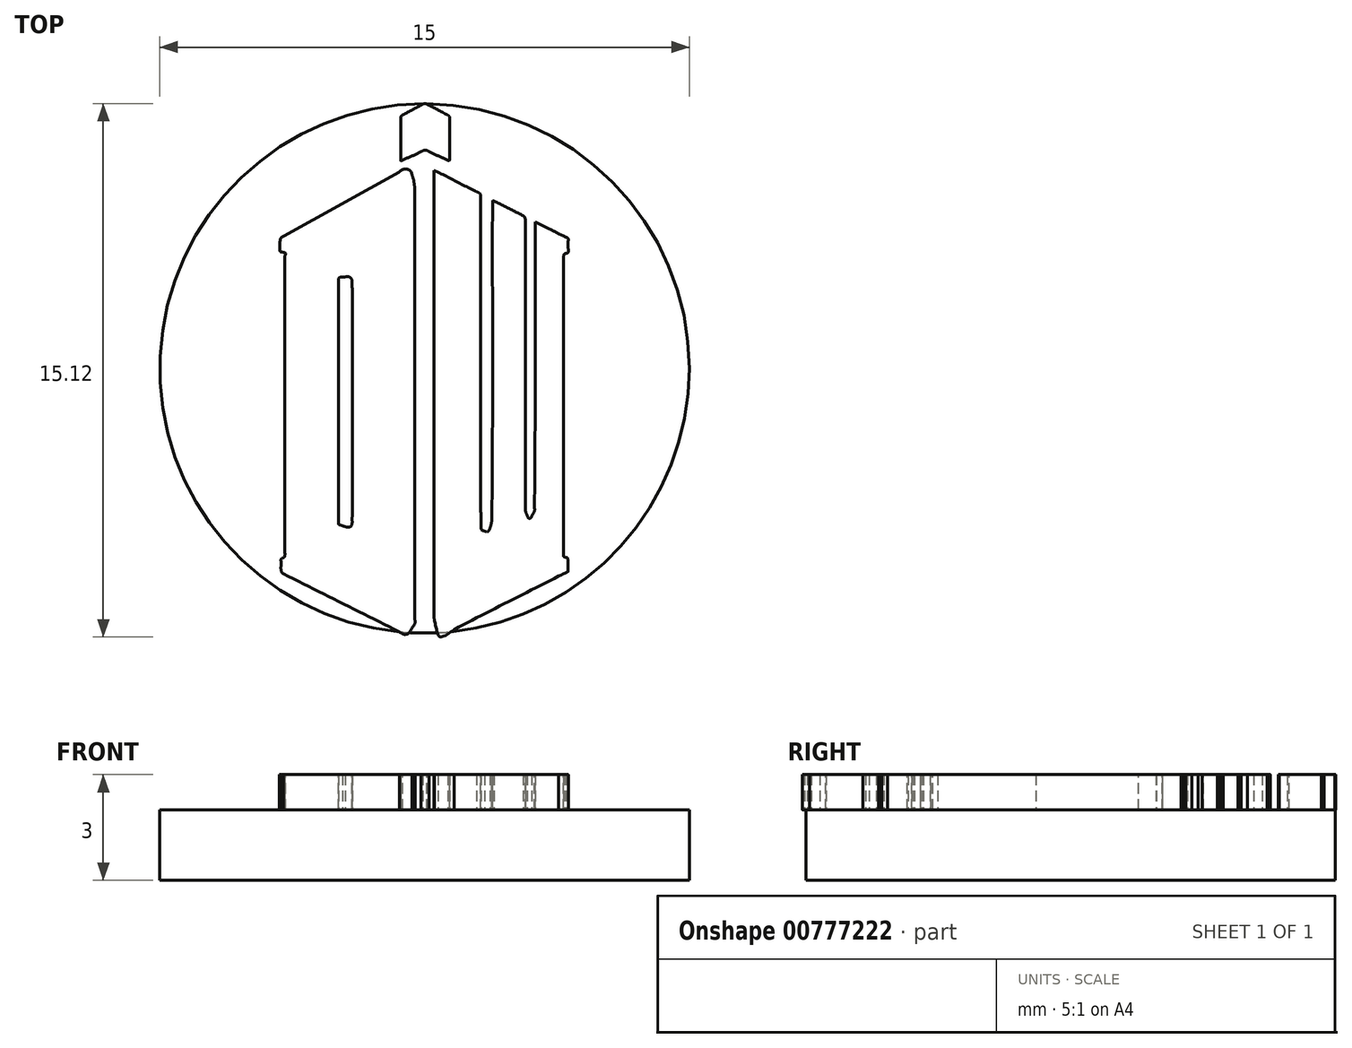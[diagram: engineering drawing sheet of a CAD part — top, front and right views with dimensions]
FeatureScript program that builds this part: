
annotation { "Feature Type Name" : "Feature", "Feature Type Description" : "" }
export const myFeature = defineFeature(function(context is Context, id is Id, definition is map)
    precondition{}
    {
        {
            var Q0;
            Q0=qCreatedBy(makeId("Top.planeOp"),FACE);
            var sketch = newSketch(context, id + "F0", { "sketchPlane" : qUnion([Q0])});
            skCircle(sketch, "E0", {"center": v(0, 0) * mm, "radius": 7.5 * mm});
            skSolve(sketch);
        }
        {
            var Q0;
            Q0=qCreatedBy(makeId("Top.planeOp"),FACE);
            var sketch = newSketch(context, id + "F1", { "sketchPlane" : qUnion([Q0])});
            skFitSpline(sketch, "E1", {"points": [v(-2.44, -4.42) * mm, v(-2.4, -4.44) * mm, v(-2.36, -4.45) * mm, v(-2.32, -4.46) * mm]});
            skFitSpline(sketch, "E2", {"points": [v(-2.32, -4.46) * mm, v(-2.15, -4.5) * mm, v(-2.07, -4.44) * mm, v(-2.05, -4.27) * mm]});
            skFitSpline(sketch, "E3", {"points": [v(-2.05, -4.27) * mm, v(-2.05, -4.15) * mm, v(-2.04, -4.03) * mm, v(-2.04, -3.9) * mm]});
            skFitSpline(sketch, "E4", {"points": [v(-2.04, -3.9) * mm, v(-2.04, -1.97) * mm, v(-2.04, -0.02) * mm, v(-2.04, 1.92) * mm]});
            skFitSpline(sketch, "E5", {"points": [v(-2.04, 1.92) * mm, v(-2.04, 2.1) * mm, v(-2.05, 2.26) * mm, v(-2.06, 2.43) * mm]});
            skFitSpline(sketch, "E6", {"points": [v(-2.06, 2.43) * mm, v(-2.06, 2.53) * mm, v(-2.15, 2.6) * mm, v(-2.24, 2.6) * mm]});
            skFitSpline(sketch, "E7", {"points": [v(-2.24, 2.6) * mm, v(-2.39, 2.58) * mm, v(-2.44, 2.54) * mm, v(-2.44, 2.42) * mm]});
            skFitSpline(sketch, "E8", {"points": [v(-2.44, 2.42) * mm, v(-2.44, 0.18) * mm, v(-2.44, -2.06) * mm, v(-2.44, -4.3) * mm]});
            skFitSpline(sketch, "E9", {"points": [v(-2.44, -4.3) * mm, v(-2.44, -4.34) * mm, v(-2.44, -4.38) * mm, v(-2.44, -4.42) * mm]});
            skFitSpline(sketch, "E10", {"points": [v(-0.28, -0.99) * mm, v(-0.28, -2.97) * mm, v(-0.28, -4.95) * mm, v(-0.28, -6.93) * mm]});
            skFitSpline(sketch, "E11", {"points": [v(-0.28, -6.93) * mm, v(-0.28, -7.07) * mm, v(-0.27, -7.22) * mm, v(-0.35, -7.35) * mm]});
            skFitSpline(sketch, "E12", {"points": [v(-0.35, -7.35) * mm, v(-0.44, -7.5) * mm, v(-0.56, -7.54) * mm, v(-0.72, -7.46) * mm]});
            skFitSpline(sketch, "E13", {"points": [v(-0.72, -7.46) * mm, v(-1.81, -6.92) * mm, v(-2.9, -6.37) * mm, v(-4, -5.82) * mm]});
            skFitSpline(sketch, "E14", {"points": [v(-4, -5.82) * mm, v(-4.03, -5.8) * mm, v(-4.06, -5.75) * mm, v(-4.06, -5.71) * mm]});
            skFitSpline(sketch, "E15", {"points": [v(-4.06, -5.71) * mm, v(-4.07, -5.65) * mm, v(-4.06, -5.58) * mm, v(-4.07, -5.51) * mm]});
            skFitSpline(sketch, "E16", {"points": [v(-4.07, -5.51) * mm, v(-4.07, -5.45) * mm, v(-4.06, -5.4) * mm, v(-4, -5.37) * mm]});
            skFitSpline(sketch, "E17", {"points": [v(-4, -5.37) * mm, v(-3.98, -5.36) * mm, v(-3.97, -5.32) * mm, v(-3.96, -5.3) * mm]});
            skFitSpline(sketch, "E18", {"points": [v(-3.96, -5.3) * mm, v(-3.95, -5.26) * mm, v(-3.96, -5.23) * mm, v(-3.96, -5.2) * mm]});
            skFitSpline(sketch, "E19", {"points": [v(-3.96, -5.2) * mm, v(-3.96, -2.43) * mm, v(-3.96, 0.34) * mm, v(-3.96, 3.11) * mm]});
            skFitSpline(sketch, "E20", {"points": [v(-3.96, 3.11) * mm, v(-3.96, 3.19) * mm, v(-3.94, 3.26) * mm, v(-4.04, 3.3) * mm]});
            skFitSpline(sketch, "E21", {"points": [v(-4.04, 3.3) * mm, v(-4.1, 3.32) * mm, v(-4.07, 3.7) * mm, v(-4.02, 3.73) * mm]});
            skFitSpline(sketch, "E22", {"points": [v(-4.02, 3.73) * mm, v(-4, 3.74) * mm, v(-4, 3.75) * mm, v(-3.97, 3.76) * mm]});
            skFitSpline(sketch, "E23", {"points": [v(-3.97, 3.76) * mm, v(-2.9, 4.36) * mm, v(-1.8, 4.96) * mm, v(-0.72, 5.56) * mm]});
            skFitSpline(sketch, "E24", {"points": [v(-0.72, 5.56) * mm, v(-0.56, 5.65) * mm, v(-0.4, 5.6) * mm, v(-0.34, 5.43) * mm]});
            skFitSpline(sketch, "E25", {"points": [v(-0.34, 5.43) * mm, v(-0.31, 5.35) * mm, v(-0.3, 5.26) * mm, v(-0.29, 5.18) * mm]});
            skFitSpline(sketch, "E26", {"points": [v(-0.29, 5.18) * mm, v(-0.28, 5.12) * mm, v(-0.28, 5.05) * mm, v(-0.28, 4.99) * mm]});
            skFitSpline(sketch, "E27", {"points": [v(-0.28, 4.99) * mm, v(-0.28, 3) * mm, v(-0.28, 1) * mm, v(-0.28, -0.99) * mm]});
            skFitSpline(sketch, "E28", {"points": [v(-0.28, -0.99) * mm, v(-0.28, -0.99) * mm, v(-0.28, -0.99) * mm, v(-0.28, -0.99) * mm]});
            skFitSpline(sketch, "E29", {"points": [v(0.27, 5.62) * mm, v(0.32, 5.6) * mm, v(0.35, 5.58) * mm, v(0.38, 5.57) * mm]});
            skFitSpline(sketch, "E30", {"points": [v(0.38, 5.57) * mm, v(0.75, 5.38) * mm, v(1.11, 5.19) * mm, v(1.48, 5) * mm]});
            skFitSpline(sketch, "E31", {"points": [v(1.48, 5) * mm, v(1.56, 4.97) * mm, v(1.59, 4.93) * mm, v(1.59, 4.84) * mm]});
            skFitSpline(sketch, "E32", {"points": [v(1.59, 4.84) * mm, v(1.58, 1.97) * mm, v(1.59, -0.9) * mm, v(1.6, -3.77) * mm]});
            skFitSpline(sketch, "E33", {"points": [v(1.6, -3.77) * mm, v(1.6, -4) * mm, v(1.6, -4.22) * mm, v(1.6, -4.45) * mm]});
            skFitSpline(sketch, "E34", {"points": [v(1.6, -4.45) * mm, v(1.6, -4.52) * mm, v(1.62, -4.58) * mm, v(1.7, -4.6) * mm]});
            skFitSpline(sketch, "E35", {"points": [v(1.7, -4.6) * mm, v(1.78, -4.63) * mm, v(1.84, -4.57) * mm, v(1.86, -4.5) * mm]});
            skFitSpline(sketch, "E36", {"points": [v(1.86, -4.5) * mm, v(1.89, -4.41) * mm, v(1.9, -4.32) * mm, v(1.9, -4.22) * mm]});
            skFitSpline(sketch, "E37", {"points": [v(1.9, -4.22) * mm, v(1.91, -3.63) * mm, v(1.92, -3.04) * mm, v(1.92, -2.44) * mm]});
            skFitSpline(sketch, "E38", {"points": [v(1.92, -2.44) * mm, v(1.93, -0.09) * mm, v(1.92, 2.27) * mm, v(1.92, 4.62) * mm]});
            skFitSpline(sketch, "E39", {"points": [v(1.92, 4.62) * mm, v(1.92, 4.67) * mm, v(1.92, 4.7) * mm, v(1.92, 4.76) * mm]});
            skFitSpline(sketch, "E40", {"points": [v(1.92, 4.76) * mm, v(1.94, 4.75) * mm, v(1.96, 4.75) * mm, v(1.97, 4.75) * mm]});
            skFitSpline(sketch, "E41", {"points": [v(1.97, 4.75) * mm, v(2.25, 4.6) * mm, v(2.52, 4.47) * mm, v(2.8, 4.33) * mm]});
            skFitSpline(sketch, "E42", {"points": [v(2.8, 4.33) * mm, v(2.83, 4.3) * mm, v(2.84, 4.26) * mm, v(2.86, 4.23) * mm]});
            skFitSpline(sketch, "E43", {"points": [v(2.86, 4.23) * mm, v(2.87, 4.2) * mm, v(2.86, 4.18) * mm, v(2.86, 4.15) * mm]});
            skFitSpline(sketch, "E44", {"points": [v(2.86, 4.15) * mm, v(2.86, 1.44) * mm, v(2.86, -1.28) * mm, v(2.86, -3.99) * mm]});
            skFitSpline(sketch, "E45", {"points": [v(2.86, -3.99) * mm, v(2.86, -4.05) * mm, v(2.89, -4.12) * mm, v(2.91, -4.17) * mm]});
            skFitSpline(sketch, "E46", {"points": [v(2.91, -4.17) * mm, v(2.94, -4.24) * mm, v(3, -4.24) * mm, v(3.04, -4.19) * mm]});
            skFitSpline(sketch, "E47", {"points": [v(3.04, -4.19) * mm, v(3.08, -4.12) * mm, v(3.12, -4.04) * mm, v(3.12, -3.96) * mm]});
            skFitSpline(sketch, "E48", {"points": [v(3.12, -3.96) * mm, v(3.13, -2.6) * mm, v(3.13, -1.22) * mm, v(3.14, 0.15) * mm]});
            skFitSpline(sketch, "E49", {"points": [v(3.14, 0.15) * mm, v(3.14, 1.44) * mm, v(3.14, 2.73) * mm, v(3.14, 4.02) * mm]});
            skFitSpline(sketch, "E50", {"points": [v(3.14, 4.02) * mm, v(3.14, 4.06) * mm, v(3.14, 4.1) * mm, v(3.14, 4.15) * mm]});
            skFitSpline(sketch, "E51", {"points": [v(3.14, 4.15) * mm, v(3.27, 4.09) * mm, v(3.4, 4.02) * mm, v(3.52, 3.96) * mm]});
            skFitSpline(sketch, "E52", {"points": [v(3.52, 3.96) * mm, v(3.68, 3.88) * mm, v(3.84, 3.8) * mm, v(4, 3.72) * mm]});
            skFitSpline(sketch, "E53", {"points": [v(4, 3.72) * mm, v(4.05, 3.7) * mm, v(4.07, 3.67) * mm, v(4.07, 3.6) * mm]});
            skFitSpline(sketch, "E54", {"points": [v(4.07, 3.6) * mm, v(4.06, 3.55) * mm, v(4.06, 3.49) * mm, v(4.07, 3.43) * mm]});
            skFitSpline(sketch, "E55", {"points": [v(4.07, 3.43) * mm, v(4.07, 3.35) * mm, v(4.07, 3.29) * mm, v(3.98, 3.25) * mm]});
            skFitSpline(sketch, "E56", {"points": [v(3.98, 3.25) * mm, v(3.96, 3.25) * mm, v(3.95, 3.22) * mm, v(3.94, 3.2) * mm]});
            skFitSpline(sketch, "E57", {"points": [v(3.94, 3.2) * mm, v(3.94, 3.17) * mm, v(3.94, 3.15) * mm, v(3.94, 3.12) * mm]});
            skFitSpline(sketch, "E58", {"points": [v(3.94, 3.12) * mm, v(3.94, 0.35) * mm, v(3.94, -2.42) * mm, v(3.94, -5.2) * mm]});
            skFitSpline(sketch, "E59", {"points": [v(3.94, -5.2) * mm, v(3.94, -5.27) * mm, v(3.94, -5.33) * mm, v(4.03, -5.36) * mm]});
            skFitSpline(sketch, "E60", {"points": [v(4.03, -5.36) * mm, v(4.05, -5.36) * mm, v(4.06, -5.4) * mm, v(4.07, -5.42) * mm]});
            skFitSpline(sketch, "E61", {"points": [v(4.07, -5.42) * mm, v(4.07, -5.42) * mm, v(4.07, -5.43) * mm, v(4.07, -5.44) * mm]});
            skFitSpline(sketch, "E62", {"points": [v(4.07, -5.44) * mm, v(4.07, -5.74) * mm, v(4.07, -5.75) * mm, v(3.8, -5.88) * mm]});
            skFitSpline(sketch, "E63", {"points": [v(3.8, -5.88) * mm, v(2.81, -6.39) * mm, v(1.82, -6.89) * mm, v(0.84, -7.4) * mm]});
            skFitSpline(sketch, "E64", {"points": [v(0.84, -7.4) * mm, v(0.44, -7.6) * mm, v(0.35, -7.42) * mm, v(0.28, -7.1) * mm]});
            skFitSpline(sketch, "E65", {"points": [v(0.28, -7.1) * mm, v(0.27, -7.06) * mm, v(0.27, -7) * mm, v(0.27, -6.95) * mm]});
            skFitSpline(sketch, "E66", {"points": [v(0.27, -6.95) * mm, v(0.27, -2.8) * mm, v(0.27, 1.36) * mm, v(0.27, 5.5) * mm]});
            skFitSpline(sketch, "E67", {"points": [v(0.27, 5.5) * mm, v(0.27, 5.54) * mm, v(0.27, 5.57) * mm, v(0.27, 5.62) * mm]});
            skFitSpline(sketch, "E68", {"points": [v(-0.68, 5.88) * mm, v(-0.68, 6.3) * mm, v(-0.68, 6.7) * mm, v(-0.67, 7.1) * mm]});
            skFitSpline(sketch, "E69", {"points": [v(-0.67, 7.1) * mm, v(-0.67, 7.13) * mm, v(-0.64, 7.17) * mm, v(-0.62, 7.18) * mm]});
            skFitSpline(sketch, "E70", {"points": [v(-0.62, 7.18) * mm, v(-0.43, 7.29) * mm, v(-0.24, 7.39) * mm, v(-0.05, 7.49) * mm]});
            skFitSpline(sketch, "E71", {"points": [v(-0.05, 7.49) * mm, v(-0.02, 7.5) * mm, v(0.04, 7.5) * mm, v(0.07, 7.49) * mm]});
            skFitSpline(sketch, "E72", {"points": [v(0.07, 7.49) * mm, v(0.27, 7.39) * mm, v(0.46, 7.28) * mm, v(0.66, 7.18) * mm]});
            skFitSpline(sketch, "E73", {"points": [v(0.66, 7.18) * mm, v(0.68, 7.16) * mm, v(0.71, 7.12) * mm, v(0.71, 7.1) * mm]});
            skFitSpline(sketch, "E74", {"points": [v(0.71, 7.1) * mm, v(0.71, 6.7) * mm, v(0.71, 6.3) * mm, v(0.71, 5.91) * mm]});
            skFitSpline(sketch, "E75", {"points": [v(0.71, 5.91) * mm, v(0.71, 5.9) * mm, v(0.7, 5.9) * mm, v(0.7, 5.89) * mm]});
            skFitSpline(sketch, "E76", {"points": [v(0.7, 5.89) * mm, v(0.51, 5.97) * mm, v(0.32, 6.05) * mm, v(0.13, 6.14) * mm]});
            skFitSpline(sketch, "E77", {"points": [v(0.13, 6.14) * mm, v(0.05, 6.18) * mm, v(-0.02, 6.19) * mm, v(-0.1, 6.14) * mm]});
            skFitSpline(sketch, "E78", {"points": [v(-0.1, 6.14) * mm, v(-0.28, 6.05) * mm, v(-0.48, 5.97) * mm, v(-0.68, 5.88) * mm]});
            skSolve(sketch);
        }
        {
            var Q0;
            Q0 = qSketchRegion(id + "F0", true);
            extrude(context, id + "F2", {"entities" : qUnion([Q0]), "oppositeDirection" : true, "depth" : 2 * mm, "offsetDistance" : 25 * mm});
        }
        {
            var Q0;
            Q0 = qSketchRegion(id + "F1", true);
            extrude(context, id + "F3", {"entities" : qUnion([Q0]), "operationType" : NewBodyOperationType.ADD, "depth" : 1 * mm, "offsetDistance" : 25 * mm});
        }
    });
